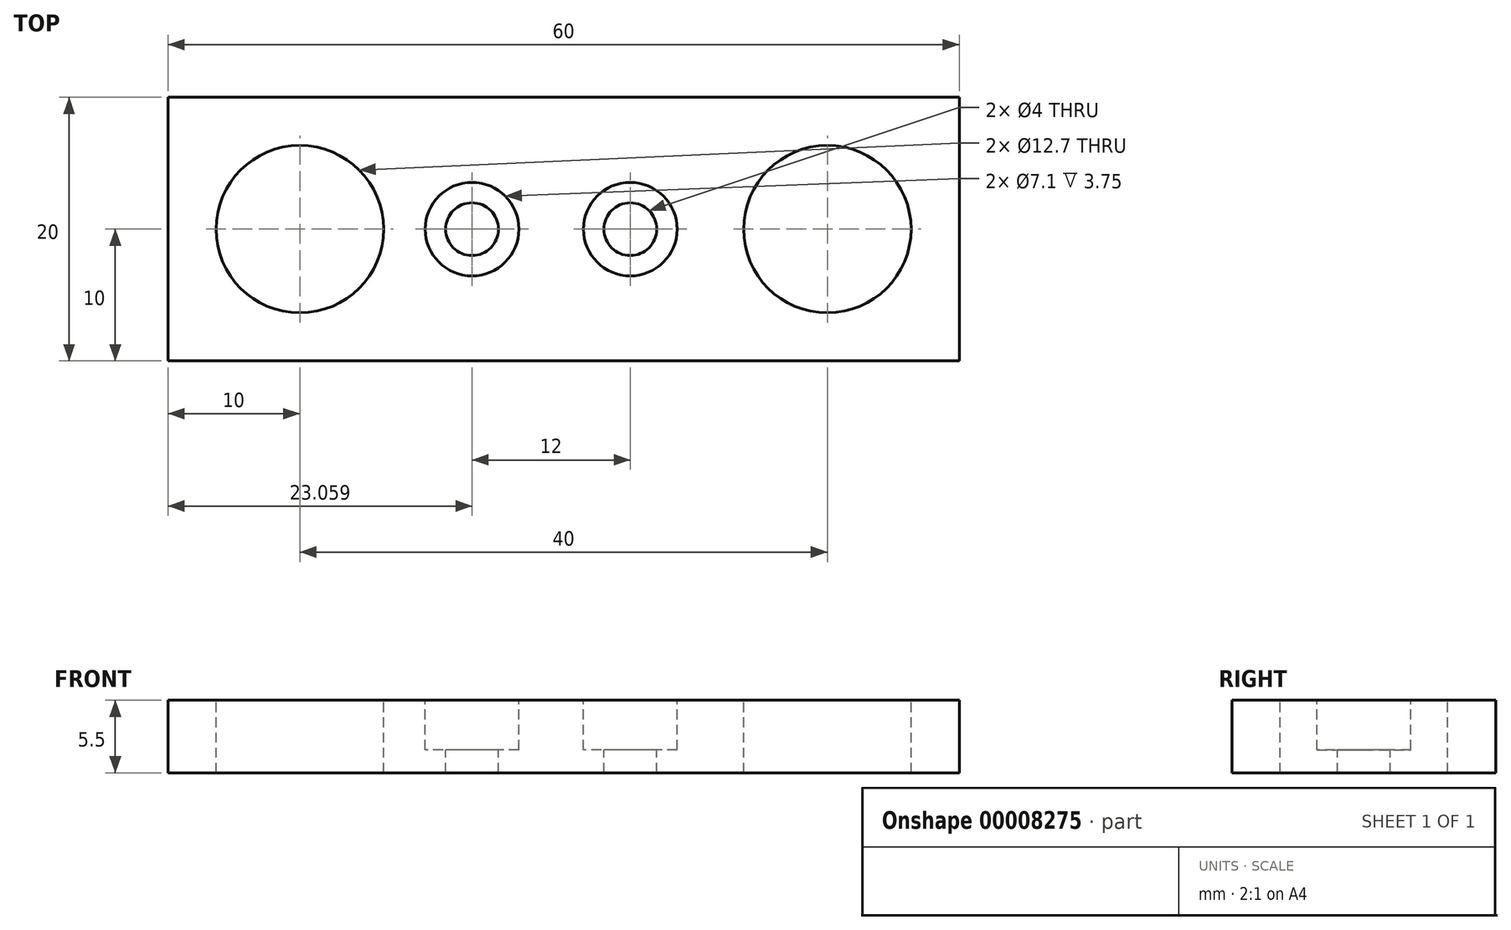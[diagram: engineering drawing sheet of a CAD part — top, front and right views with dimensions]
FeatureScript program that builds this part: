
annotation { "Feature Type Name" : "Feature", "Feature Type Description" : "" }
export const myFeature = defineFeature(function(context is Context, id is Id, definition is map)
    precondition{}
    {
        {
            var Q0;
            Q0=qCreatedBy(makeId("Top.planeOp"),FACE);
            var sketch = newSketch(context, id + "F0", { "sketchPlane" : qUnion([Q0])});
            skLineSegment(sketch, "E0.rect.bottom", {"start": v(30, -10) * mm, "end": v(-30, -10) * mm});
            skLineSegment(sketch, "E0.rect.top", {"start": v(30, 10) * mm, "end": v(-30, 10) * mm});
            skLineSegment(sketch, "E0.rect.left", {"start": v(30, -10) * mm, "end": v(30, 10) * mm});
            skLineSegment(sketch, "E0.rect.right", {"start": v(-30, -10) * mm, "end": v(-30, 10) * mm});
            skPoint(sketch, "E0.rect.middle", {"position": v(0, 0) * mm});
            skSolve(sketch);
        }
        {
            var Q0;
            Q0=makeQuery(id+"F0.imprint","IMPRINT",FACE,{"disambiguationData":[TD([[makeQuery(id+"F0.imprint","IMPRINT",EDGE,{"derivedFrom":sQuery(id+"F0.wireOp",EDGE,"E0.rect.bottom")}),-1.0]])]});
            extrude(context, id + "F1", {"entities" : qUnion([Q0]), "depth" : 5.5 * mm});
        }
        {
            var Q0;
            Q0=makeQuery(id+"F1.opExtrude","CAP_FACE",FACE,{"disambiguationData":[OSD([sQuery(id+"F0.wireOp",EDGE,"E0.rect.bottom"),sQuery(id+"F0.wireOp",EDGE,"E0.rect.top"),sQuery(id+"F0.wireOp",EDGE,"E0.rect.left"),sQuery(id+"F0.wireOp",EDGE,"E0.rect.right")])],"isStart":false});
            var sketch = newSketch(context, id + "F2", { "sketchPlane" : qUnion([Q0])});
            skLineSegment(sketch, "E1", {"start": v(-30, 0) * mm, "end": v(30, 0) * mm, "construction": true});
            skPoint(sketch, "E2", {"position": v(-20, 0) * mm});
            skPoint(sketch, "E3", {"position": v(20, 0) * mm});
            skCircle(sketch, "E4", {"center": v(-20, 0) * mm, "radius": 6.35 * mm});
            skCircle(sketch, "E5", {"center": v(20, 0) * mm, "radius": 6.35 * mm});
            skSolve(sketch);
        }
        {
            var Q0;
            Q0=makeQuery(id+"F2.imprint","IMPRINT",FACE,{"disambiguationData":[TD([[makeQuery(id+"F2.imprint","IMPRINT",EDGE,{"derivedFrom":sQuery(id+"F2.wireOp",EDGE,"E4")}),1.0]])]});
            var Q1;
            Q1=makeQuery(id+"F2.imprint","IMPRINT",FACE,{"disambiguationData":[TD([[makeQuery(id+"F2.imprint","IMPRINT",EDGE,{"derivedFrom":sQuery(id+"F2.wireOp",EDGE,"E5")}),1.0]])]});
            extrude(context, id + "F3", {"entities" : qUnion([Q0, Q1]), "operationType" : NewBodyOperationType.REMOVE, "oppositeDirection" : true, "depth" : 5.5 * mm});
        }
        {
            var Q0;
            Q0=makeQuery(id+"F1.opExtrude","CAP_FACE",FACE,{"disambiguationData":[OSD([sQuery(id+"F0.wireOp",EDGE,"E0.rect.bottom"),sQuery(id+"F0.wireOp",EDGE,"E0.rect.top"),sQuery(id+"F0.wireOp",EDGE,"E0.rect.left"),sQuery(id+"F0.wireOp",EDGE,"E0.rect.right")])],"isStart":false});
            var sketch = newSketch(context, id + "F4", { "sketchPlane" : qUnion([Q0])});
            skLineSegment(sketch, "E6", {"start": v(-0.94, 0) * mm, "end": v(-6.94, 0) * mm, "construction": true});
            skLineSegment(sketch, "E7", {"start": v(-0.94, 0) * mm, "end": v(5.06, 0) * mm, "construction": true});
            skCircle(sketch, "E8", {"center": v(-6.94, 0) * mm, "radius": 3.55 * mm});
            skCircle(sketch, "E9", {"center": v(5.06, 0) * mm, "radius": 3.55 * mm});
            skCircle(sketch, "E10", {"center": v(-6.94, 0) * mm, "radius": 2 * mm});
            skCircle(sketch, "E11", {"center": v(5.06, 0) * mm, "radius": 2 * mm});
            skLineSegment(sketch, "E12.0", {"start": v(-30, 0) * mm, "end": v(30, 0) * mm, "construction": true});
            skSolve(sketch);
        }
        {
            var Q0;
            Q0=makeQuery(id+"F4.imprint","IMPRINT",FACE,{"disambiguationData":[TD([[makeQuery(id+"F4.imprint","IMPRINT",EDGE,{"derivedFrom":sQuery(id+"F4.wireOp",EDGE,"E10")}),1.0]])]});
            var Q1;
            Q1=makeQuery(id+"F4.imprint","IMPRINT",FACE,{"disambiguationData":[TD([[makeQuery(id+"F4.imprint","IMPRINT",EDGE,{"derivedFrom":sQuery(id+"F4.wireOp",EDGE,"E11")}),1.0]])]});
            var Q2;
            Q2=sQuery(id+"F4.wireOp",EDGE,"E10");
            var Q3;
            Q3=sQuery(id+"F4.wireOp",EDGE,"E11");
            extrude(context, id + "F5", {"entities" : qUnion([Q0, Q1]), "operationType" : NewBodyOperationType.REMOVE, "surfaceEntities" : qUnion([Q2, Q3]), "oppositeDirection" : true, "depth" : 25 * mm});
        }
        {
            var Q0;
            Q0=makeQuery(id+"F4.imprint","IMPRINT",FACE,{"disambiguationData":[TD([[makeQuery(id+"F4.imprint","IMPRINT",EDGE,{"derivedFrom":sQuery(id+"F4.wireOp",EDGE,"E8")}),1.0]])]});
            var Q1;
            Q1=makeQuery(id+"F4.imprint","IMPRINT",FACE,{"disambiguationData":[TD([[makeQuery(id+"F4.imprint","IMPRINT",EDGE,{"derivedFrom":sQuery(id+"F4.wireOp",EDGE,"E9")}),1.0]])]});
            extrude(context, id + "F6", {"entities" : qUnion([Q0, Q1]), "operationType" : NewBodyOperationType.REMOVE, "oppositeDirection" : true, "depth" : 3.75 * mm});
        }
    });
